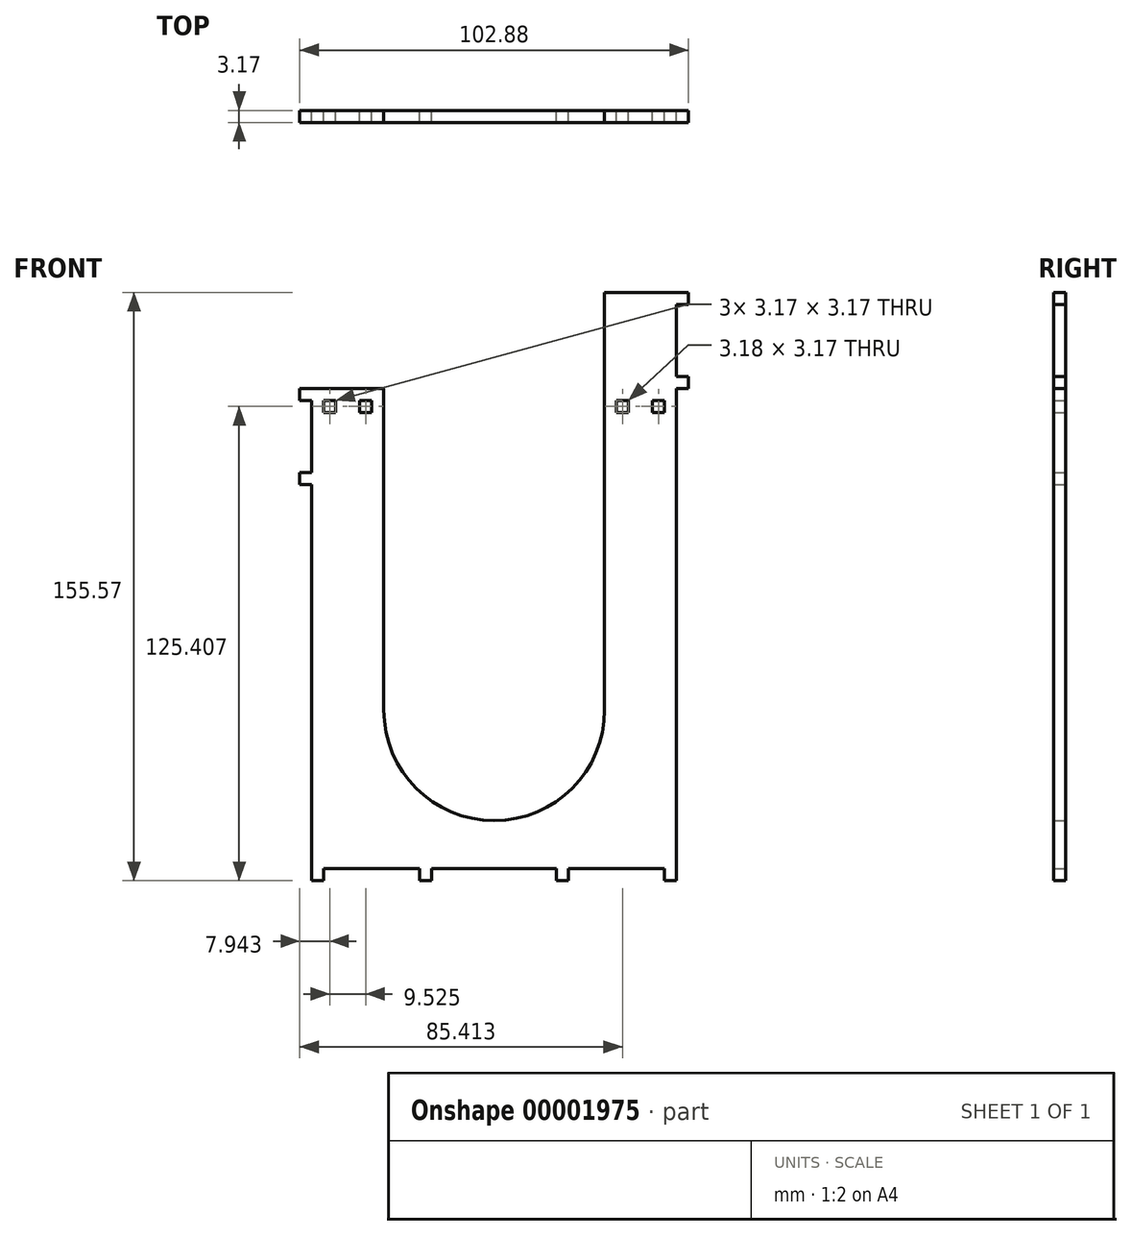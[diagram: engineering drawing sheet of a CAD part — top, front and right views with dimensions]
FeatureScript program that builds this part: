
annotation { "Feature Type Name" : "Feature", "Feature Type Description" : "" }
export const myFeature = defineFeature(function(context is Context, id is Id, definition is map)
    precondition{}
    {
        {
            var Q0;
            Q0=qCreatedBy(makeId("Front.planeOp"),FACE);
            var sketch = newSketch(context, id + "F0", { "sketchPlane" : qUnion([Q0])});
            skLineSegment(sketch, "E0", {"start": v(0, 0) * mm, "end": v(0, 127) * mm});
            skLineSegment(sketch, "E1", {"start": v(-19.05, 152.4) * mm, "end": v(-19.05, 41.91) * mm});
            skLineSegment(sketch, "E2", {"start": v(-3.18, 0) * mm, "end": v(-28.58, 0) * mm});
            skLineSegment(sketch, "E3", {"start": v(0, 0) * mm, "end": v(0, -3.18) * mm});
            skLineSegment(sketch, "E4", {"start": v(0, -3.18) * mm, "end": v(-3.17, -3.18) * mm});
            skLineSegment(sketch, "E5", {"start": v(-3.18, -3.18) * mm, "end": v(-3.18, 0) * mm});
            skLineSegment(sketch, "E6", {"start": v(-31.75, 0) * mm, "end": v(-31.75, -3.18) * mm});
            skLineSegment(sketch, "E7", {"start": v(-28.58, -3.18) * mm, "end": v(-31.75, -3.18) * mm});
            skLineSegment(sketch, "E8", {"start": v(-28.58, -3.18) * mm, "end": v(-28.58, 0) * mm});
            skLineSegment(sketch, "E9", {"start": v(-64.77, 0) * mm, "end": v(-64.77, -3.18) * mm});
            skLineSegment(sketch, "E10", {"start": v(-64.77, -3.18) * mm, "end": v(-67.95, -3.18) * mm});
            skLineSegment(sketch, "E11", {"start": v(-67.95, -3.18) * mm, "end": v(-67.95, 0) * mm});
            skLineSegment(sketch, "E12.trimOffspring", {"start": v(-31.75, 0) * mm, "end": v(-64.77, 0) * mm});
            skLineSegment(sketch, "E13.trimOffspring", {"start": v(-67.95, 0) * mm, "end": v(-93.35, 0) * mm});
            skPoint(sketch, "E14.visualSharp", {"position": v(-19.05, 41.91) * mm});
            skLineSegment(sketch, "E15", {"start": v(-96.52, 0) * mm, "end": v(-96.52, -3.18) * mm});
            skLineSegment(sketch, "E16", {"start": v(-96.52, -3.18) * mm, "end": v(-93.35, -3.18) * mm});
            skLineSegment(sketch, "E17", {"start": v(-93.35, -3.18) * mm, "end": v(-93.35, 0) * mm});
            skLineSegment(sketch, "E18", {"start": v(0, 130.17) * mm, "end": v(3.17, 130.17) * mm});
            skLineSegment(sketch, "E19", {"start": v(3.17, 130.17) * mm, "end": v(3.17, 127) * mm});
            skLineSegment(sketch, "E20", {"start": v(3.17, 127) * mm, "end": v(0, 127) * mm});
            skLineSegment(sketch, "E21.trimOffspring", {"start": v(0, 130.17) * mm, "end": v(0, 149.22) * mm});
            skLineSegment(sketch, "E22", {"start": v(0, 149.22) * mm, "end": v(3.17, 149.22) * mm});
            skLineSegment(sketch, "E23", {"start": v(3.17, 149.22) * mm, "end": v(3.17, 152.4) * mm});
            skLineSegment(sketch, "E24", {"start": v(3.18, 152.4) * mm, "end": v(-19.05, 152.4) * mm});
            skLineSegment(sketch, "E25", {"start": v(-96.52, 0) * mm, "end": v(-96.52, 101.6) * mm});
            skLineSegment(sketch, "E26", {"start": v(-96.52, 101.6) * mm, "end": v(-99.7, 101.6) * mm});
            skLineSegment(sketch, "E27", {"start": v(-99.7, 101.6) * mm, "end": v(-99.7, 104.77) * mm});
            skLineSegment(sketch, "E28", {"start": v(-99.7, 104.77) * mm, "end": v(-96.52, 104.77) * mm});
            skLineSegment(sketch, "E29", {"start": v(-96.52, 104.77) * mm, "end": v(-96.52, 123.82) * mm});
            skLineSegment(sketch, "E30", {"start": v(-96.52, 123.82) * mm, "end": v(-99.7, 123.82) * mm});
            skLineSegment(sketch, "E31", {"start": v(-99.7, 123.82) * mm, "end": v(-99.7, 127) * mm});
            skLineSegment(sketch, "E32", {"start": v(-99.7, 127) * mm, "end": v(-77.47, 127) * mm});
            skLineSegment(sketch, "E33", {"start": v(-77.47, 127) * mm, "end": v(-77.47, 41.91) * mm});
            skArc(sketch, "E34", {"start": v(-77.47, 41.91) * mm, "mid": v(-48.26, 12.7) * mm, "end": v(-19.05, 41.9) * mm});
            skLineSegment(sketch, "E35.bottom", {"start": v(-93.35, 123.82) * mm, "end": v(-90.17, 123.82) * mm});
            skLineSegment(sketch, "E35.top", {"start": v(-93.35, 120.65) * mm, "end": v(-90.17, 120.65) * mm});
            skLineSegment(sketch, "E35.left", {"start": v(-93.35, 123.82) * mm, "end": v(-93.35, 120.65) * mm});
            skLineSegment(sketch, "E35.right", {"start": v(-90.17, 123.82) * mm, "end": v(-90.17, 120.65) * mm});
            skLineSegment(sketch, "E36.bottom", {"start": v(-83.82, 123.82) * mm, "end": v(-80.65, 123.82) * mm});
            skLineSegment(sketch, "E36.top", {"start": v(-83.82, 120.65) * mm, "end": v(-80.65, 120.65) * mm});
            skLineSegment(sketch, "E36.left", {"start": v(-83.82, 123.82) * mm, "end": v(-83.82, 120.65) * mm});
            skLineSegment(sketch, "E36.right", {"start": v(-80.65, 123.82) * mm, "end": v(-80.65, 120.65) * mm});
            skLineSegment(sketch, "E37", {"start": v(-48.26, 41.91) * mm, "end": v(-48.26, 153.91) * mm, "construction": true});
            skLineSegment(sketch, "E38.0.MirrorCS", {"start": v(-3.17, 123.82) * mm, "end": v(-3.17, 120.65) * mm});
            skLineSegment(sketch, "E38.1.MirrorCS", {"start": v(-12.7, 120.65) * mm, "end": v(-15.87, 120.65) * mm});
            skLineSegment(sketch, "E38.2.MirrorCS", {"start": v(-12.7, 123.82) * mm, "end": v(-12.7, 120.65) * mm});
            skLineSegment(sketch, "E38.3.MirrorCS", {"start": v(-15.87, 123.83) * mm, "end": v(-15.87, 120.65) * mm});
            skLineSegment(sketch, "E38.4.MirrorCS", {"start": v(-3.17, 120.65) * mm, "end": v(-6.35, 120.65) * mm});
            skLineSegment(sketch, "E38.5.MirrorCS", {"start": v(-12.7, 123.82) * mm, "end": v(-15.87, 123.82) * mm});
            skLineSegment(sketch, "E38.6.MirrorCS", {"start": v(-6.35, 123.82) * mm, "end": v(-6.35, 120.65) * mm});
            skLineSegment(sketch, "E38.7.MirrorCS", {"start": v(-3.17, 123.82) * mm, "end": v(-6.35, 123.82) * mm});
            skSolve(sketch);
        }
        {
            var Q0;
            Q0=makeQuery(id+"F0.imprint","IMPRINT",FACE,{"disambiguationData":[TD([[makeQuery(id+"F0.imprint","IMPRINT",EDGE,{"derivedFrom":sQuery(id+"F0.wireOp",EDGE,"E1")}),1.0]])]});
            extrude(context, id + "F1", {"entities" : qUnion([Q0]), "depth" : 3.17 * mm});
        }
    });
